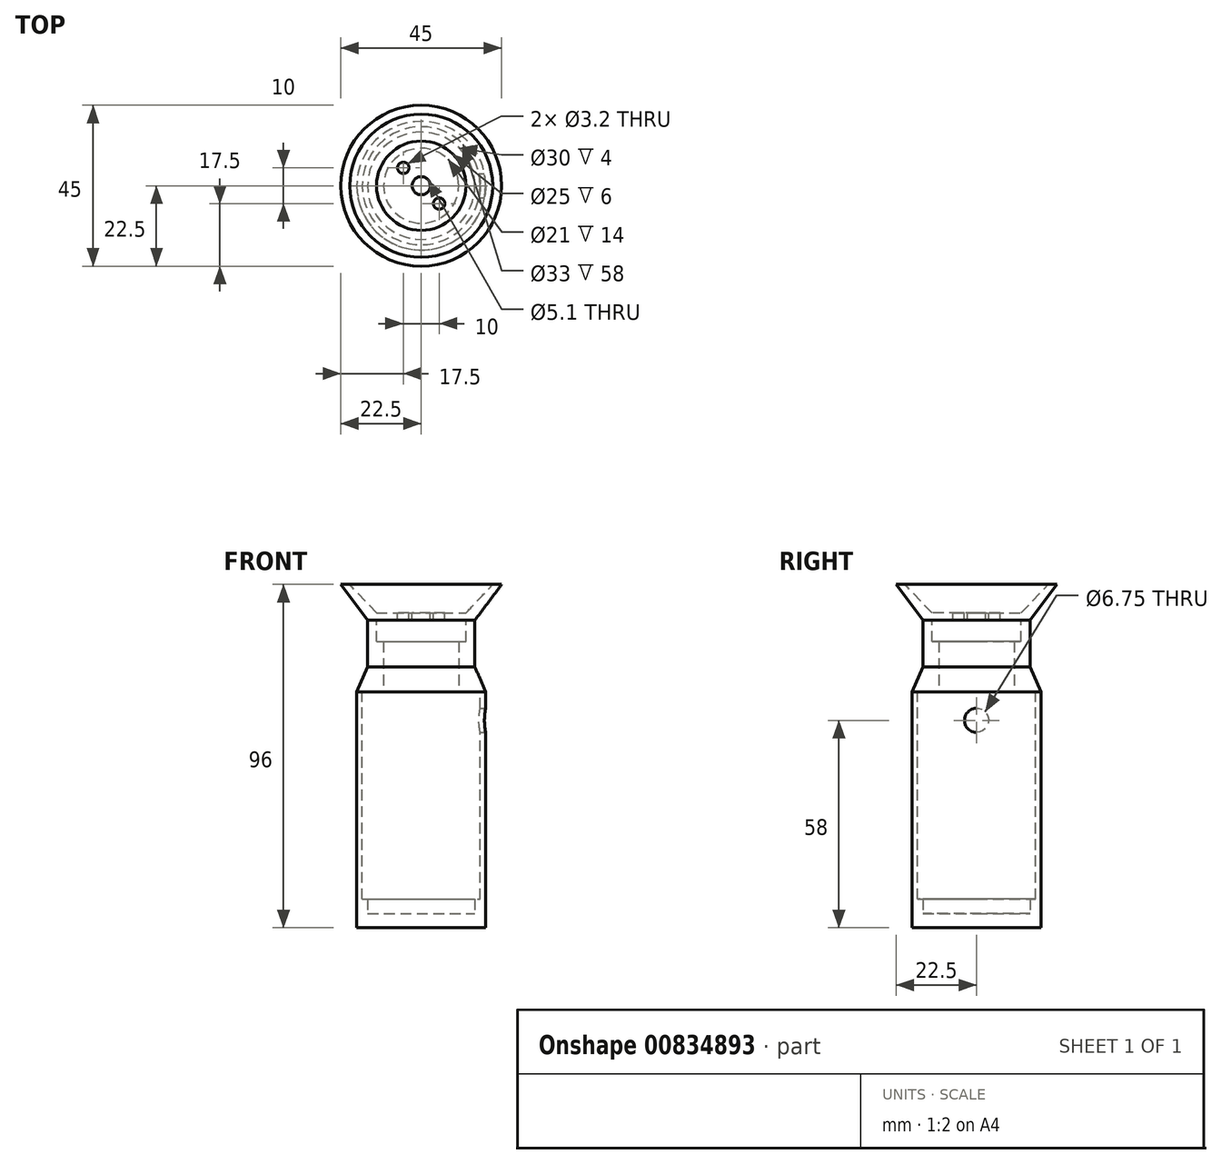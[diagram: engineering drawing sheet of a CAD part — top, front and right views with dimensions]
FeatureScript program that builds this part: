
annotation { "Feature Type Name" : "Feature", "Feature Type Description" : "" }
export const myFeature = defineFeature(function(context is Context, id is Id, definition is map)
    precondition{}
    {
        {
            var Q0;
            Q0=qCreatedBy(makeId("Top.planeOp"),FACE);
            var sketch = newSketch(context, id + "F0", { "sketchPlane" : qUnion([Q0])});
            skCircle(sketch, "E0", {"center": v(0, 0) * mm, "radius": 15 * mm});
            skSolve(sketch);
        }
        {
            var Q0;
            Q0=qCreatedBy(makeId("Top.planeOp"),FACE);
            cPlane(context, id + "F1", {"entities" : qUnion([Q0]), "cplaneType" : CPlaneType.OFFSET, "offset" : 10 * mm, "width" : 150 * mm, "height" : 150 * mm});
        }
        {
            var Q0;
            Q0=qCreatedBy(id+"F1.planeOp",FACE);
            var sketch = newSketch(context, id + "F2", { "sketchPlane" : qUnion([Q0])});
            skCircle(sketch, "E1", {"center": v(0, 0) * mm, "radius": 22.5 * mm});
            skSolve(sketch);
        }
        {
            var Q0;
            Q0=makeQuery(id+"F2.imprint","IMPRINT",FACE,{"disambiguationData":[TD([[makeQuery(id+"F2.imprint","IMPRINT",EDGE,{"derivedFrom":sQuery(id+"F2.wireOp",EDGE,"E1")}),1.0]])]});
            var Q1;
            Q1=makeQuery(id+"F0.imprint","IMPRINT",FACE,{"disambiguationData":[TD([[makeQuery(id+"F0.imprint","IMPRINT",EDGE,{"derivedFrom":sQuery(id+"F0.wireOp",EDGE,"E0")}),1.0]])]});
            loft(context, id + "F3", {"sheetProfilesArray" : [{ "sheetProfileEntities" : qUnion([Q0]) }, { "sheetProfileEntities" : qUnion([Q1]) }]});
        }
        {
            var Q0;
            Q0=makeQuery(id+"F3.opLoft","CAP_FACE",FACE,{"disambiguationData":[OSD([makeQuery(id+"F2.imprint","IMPRINT",FACE,{"disambiguationData":[TD([[makeQuery(id+"F2.imprint","IMPRINT",EDGE,{"derivedFrom":sQuery(id+"F2.wireOp",EDGE,"E1")}),1.0]])]})])],"isStart":true});
            var sketch = newSketch(context, id + "F4", { "sketchPlane" : qUnion([Q0])});
            skCircle(sketch, "E2", {"center": v(0, 0) * mm, "radius": 20 * mm});
            skSolve(sketch);
        }
        {
            var Q0;
            Q0=makeQuery(id+"F3.opLoft","CAP_FACE",FACE,{"disambiguationData":[OSD([makeQuery(id+"F0.imprint","IMPRINT",FACE,{"disambiguationData":[TD([[makeQuery(id+"F0.imprint","IMPRINT",EDGE,{"derivedFrom":sQuery(id+"F0.wireOp",EDGE,"E0")}),1.0]])]})])],"isStart":true});
            cPlane(context, id + "F5", {"entities" : qUnion([Q0]), "cplaneType" : CPlaneType.OFFSET, "offset" : 2 * mm, "oppositeDirection" : true, "width" : 150 * mm, "height" : 150 * mm});
        }
        {
            var Q0;
            Q0=qCreatedBy(id+"F5.planeOp",FACE);
            var sketch = newSketch(context, id + "F6", { "sketchPlane" : qUnion([Q0])});
            skCircle(sketch, "E3", {"center": v(0, 0) * mm, "radius": 12.5 * mm});
            skSolve(sketch);
        }
        {
            var Q1;
            Q1 = qSketchRegion(id + "F6", true);
            var Q2;
            Q2 = qSketchRegion(id + "F4", true);
            loft(context, id + "F7", {"operationType" : NewBodyOperationType.REMOVE, "sheetProfilesArray" : [{ "sheetProfileEntities" : qUnion([Q1]) }, { "sheetProfileEntities" : qUnion([Q2]) }]});
        }
        {
            var Q0;
            Q0=makeQuery(id+"F3.opLoft","CAP_FACE",FACE,{"disambiguationData":[OSD([makeQuery(id+"F0.imprint","IMPRINT",FACE,{"disambiguationData":[TD([[makeQuery(id+"F0.imprint","IMPRINT",EDGE,{"derivedFrom":sQuery(id+"F0.wireOp",EDGE,"E0")}),1.0]])]})])],"isStart":true});
            var sketch = newSketch(context, id + "F8", { "sketchPlane" : qUnion([Q0])});
            skCircle(sketch, "E4", {"center": v(0, 0) * mm, "radius": 12.5 * mm});
            skSolve(sketch);
        }
        {
            var Q0;
            Q0=makeQuery(id+"F8.imprint","IMPRINT",FACE,{"disambiguationData":[TD([[makeQuery(id+"F8.imprint","IMPRINT",EDGE,{"derivedFrom":sQuery(id+"F8.wireOp",EDGE,"E4")}),-1.0]])]});
            extrude(context, id + "F9", {"entities" : qUnion([Q0]), "operationType" : NewBodyOperationType.ADD, "depth" : 13 * mm, "offsetDistance" : 25 * mm});
        }
        {
            var Q0;
            Q0=makeQuery(id+"F9.opExtrude","CAP_FACE",FACE,{"disambiguationData":[OSD([sQuery(id+"F0.wireOp",EDGE,"E0"),sQuery(id+"F8.wireOp",EDGE,"E4")])],"isStart":false});
            var sketch = newSketch(context, id + "F10", { "sketchPlane" : qUnion([Q0])});
            skCircle(sketch, "E5", {"center": v(0, 0) * mm, "radius": 10.5 * mm});
            skSolve(sketch);
        }
        {
            var Q0;
            Q0=makeQuery(id+"F10.imprint","IMPRINT",FACE,{"disambiguationData":[TD([[makeQuery(id+"F10.imprint","IMPRINT",EDGE,{"derivedFrom":sQuery(id+"F10.wireOp",EDGE,"E5")}),-1.0]])]});
            extrude(context, id + "F11", {"entities" : qUnion([Q0]), "oppositeDirection" : true, "depth" : 7 * mm, "offsetDistance" : 25 * mm});
        }
        {
            var Q0;
            Q0=makeQuery(id+"F11.opExtrude","CAP_FACE",FACE,{"disambiguationData":[OSD([sQuery(id+"F8.wireOp",EDGE,"E4"),sQuery(id+"F10.wireOp",EDGE,"E5")])],"isStart":true});
            var sketch = newSketch(context, id + "F12", { "sketchPlane" : qUnion([Q0])});
            skCircle(sketch, "E6", {"center": v(0, 0) * mm, "radius": 15 * mm});
            skCircle(sketch, "E7", {"center": v(0, 0) * mm, "radius": 10.5 * mm});
            skSolve(sketch);
        }
        {
            var Q0;
            Q0=qCreatedBy(makeId("Top.planeOp"),FACE);
            cPlane(context, id + "F13", {"entities" : qUnion([Q0]), "cplaneType" : CPlaneType.OFFSET, "offset" : 20 * mm, "oppositeDirection" : true, "width" : 150 * mm, "height" : 150 * mm});
        }
        {
            var Q0;
            Q0=qCreatedBy(id+"F13.planeOp",FACE);
            var sketch = newSketch(context, id + "F14", { "sketchPlane" : qUnion([Q0])});
            skCircle(sketch, "E8", {"center": v(0, 0) * mm, "radius": 18 * mm});
            skSolve(sketch);
        }
        {
            var Q0;
            Q0=makeQuery(id+"F12.imprint","IMPRINT",FACE,{"disambiguationData":[TD([[makeQuery(id+"F12.imprint","IMPRINT",EDGE,{"derivedFrom":sQuery(id+"F12.wireOp",EDGE,"E6")}),1.0]])]});
            var sketch = newSketch(context, id + "F15", { "sketchPlane" : qUnion([Q0])});
            skCircle(sketch, "E9", {"center": v(0, 0) * mm, "radius": 15 * mm});
            skSolve(sketch);
        }
        {
            var Q1;
            Q1 = qSketchRegion(id + "F14", true);
            var Q2;
            Q2 = qSketchRegion(id + "F15", true);
            loft(context, id + "F16", {"operationType" : NewBodyOperationType.ADD, "sheetProfilesArray" : [{ "sheetProfileEntities" : qUnion([Q1]) }, { "sheetProfileEntities" : qUnion([Q2]) }]});
        }
        {
            var Q0;
            Q0=makeQuery(id+"F16.opLoft","CAP_FACE",FACE,{"disambiguationData":[OSD([makeQuery(id+"F14.imprint","IMPRINT",FACE,{"disambiguationData":[TD([[makeQuery(id+"F14.imprint","IMPRINT",EDGE,{"derivedFrom":sQuery(id+"F14.wireOp",EDGE,"E8")}),1.0]])]})])],"isStart":true});
            var sketch = newSketch(context, id + "F17", { "sketchPlane" : qUnion([Q0])});
            skCircle(sketch, "E10", {"center": v(0, 0) * mm, "radius": 10.5 * mm});
            skSolve(sketch);
        }
        {
            var Q0;
            Q0=makeQuery(id+"F17.imprint","IMPRINT",FACE,{"disambiguationData":[TD([[makeQuery(id+"F17.imprint","IMPRINT",EDGE,{"derivedFrom":sQuery(id+"F17.wireOp",EDGE,"E10")}),1.0]])]});
            var Q1;
            Q1=sQuery(id+"F12.wireOp",EDGE,"E7");
            extrude(context, id + "F18", {"entities" : qUnion([Q0]), "operationType" : NewBodyOperationType.REMOVE, "surfaceOperationType" : NewSurfaceOperationType.ADD, "surfaceEntities" : qUnion([Q1]), "oppositeDirection" : true, "depth" : 10 * mm, "offsetDistance" : 25 * mm});
        }
        {
            var Q0;
            Q0=makeQuery(id+"F16.opLoft","CAP_FACE",FACE,{"disambiguationData":[OSD([makeQuery(id+"F14.imprint","IMPRINT",FACE,{"disambiguationData":[TD([[makeQuery(id+"F14.imprint","IMPRINT",EDGE,{"derivedFrom":sQuery(id+"F14.wireOp",EDGE,"E8")}),1.0]])]})])],"isStart":true});
            var sketch = newSketch(context, id + "F19", { "sketchPlane" : qUnion([Q0])});
            skCircle(sketch, "E11", {"center": v(0, 0) * mm, "radius": 16.5 * mm});
            skSolve(sketch);
        }
        {
            var Q0;
            Q0=makeQuery(id+"F19.imprint","IMPRINT",FACE,{"disambiguationData":[TD([[makeQuery(id+"F19.imprint","IMPRINT",EDGE,{"derivedFrom":sQuery(id+"F19.wireOp",EDGE,"E11")}),-1.0]])]});
            extrude(context, id + "F20", {"entities" : qUnion([Q0]), "operationType" : NewBodyOperationType.ADD, "depth" : 62 * mm, "offsetDistance" : 25 * mm});
        }
        {
            var Q0;
            Q0=makeQuery(id+"F20.opExtrude","CAP_FACE",FACE,{"disambiguationData":[OSD([sQuery(id+"F14.wireOp",EDGE,"E8"),sQuery(id+"F19.wireOp",EDGE,"E11")])],"isStart":false});
            var sketch = newSketch(context, id + "F21", { "sketchPlane" : qUnion([Q0])});
            skCircle(sketch, "E12", {"center": v(0, 0) * mm, "radius": 15 * mm});
            skSolve(sketch);
        }
        {
            var Q0;
            Q0=makeQuery(id+"F21.imprint","IMPRINT",FACE,{"disambiguationData":[TD([[makeQuery(id+"F21.imprint","IMPRINT",EDGE,{"derivedFrom":sQuery(id+"F21.wireOp",EDGE,"E12")}),-1.0]])]});
            extrude(context, id + "F22", {"entities" : qUnion([Q0]), "oppositeDirection" : true, "depth" : 4 * mm, "offsetDistance" : 25 * mm});
        }
        {
            var Q0;
            Q0=makeQuery(id+"F22.opExtrude","CAP_FACE",FACE,{"disambiguationData":[OSD([sQuery(id+"F19.wireOp",EDGE,"E11"),sQuery(id+"F21.wireOp",EDGE,"E12")])],"isStart":true});
            extrude(context, id + "F23", {"entities" : qUnion([Q0]), "operationType" : NewBodyOperationType.ADD, "depth" : 4 * mm, "offsetDistance" : 25 * mm});
        }
        {
            var Q0;
            Q0=makeQuery(id+"F23.opExtrude","CAP_FACE",FACE,{"disambiguationData":[OSD([sQuery(id+"F19.wireOp",EDGE,"E11"),sQuery(id+"F21.wireOp",EDGE,"E12")])],"isStart":false});
            var sketch = newSketch(context, id + "F24", { "sketchPlane" : qUnion([Q0])});
            skCircle(sketch, "E13", {"center": v(0, 0) * mm, "radius": 18 * mm});
            skSolve(sketch);
        }
        {
            var Q0;
            Q0=makeQuery(id+"F24.imprint","IMPRINT",FACE,{"disambiguationData":[TD([[makeQuery(id+"F24.imprint","IMPRINT",EDGE,{"derivedFrom":sQuery(id+"F24.wireOp",EDGE,"E13")}),1.0]])]});
            var Q1;
            Q1=makeQuery(id+"F24.imprint","IMPRINT",FACE,{"disambiguationData":[TD([[makeQuery(id+"F24.imprint","IMPRINT",EDGE,{"derivedFrom":makeQuery(id+"F23.opExtrude","CAP_EDGE",EDGE,{"disambiguationData":[OSD([sQuery(id+"F21.wireOp",EDGE,"E12")])],"isStart":false})}),1.0]])]});
            var Q2;
            Q2=sQuery(id+"F24.wireOp",EDGE,"E13");
            extrude(context, id + "F25", {"entities" : qUnion([Q0, Q1]), "operationType" : NewBodyOperationType.ADD, "surfaceOperationType" : NewSurfaceOperationType.ADD, "surfaceEntities" : qUnion([Q2]), "oppositeDirection" : true, "depth" : 4 * mm, "offsetDistance" : 25 * mm});
        }
        {
            var Q0;
            Q0=makeQuery(id+"F7.boolean.opBoolean","COPY",FACE,{"derivedFrom":makeQuery(id+"F7.opLoft","CAP_FACE",FACE,{"disambiguationData":[OSD([makeQuery(id+"F6.imprint","IMPRINT",FACE,{"disambiguationData":[TD([[makeQuery(id+"F6.imprint","IMPRINT",EDGE,{"derivedFrom":sQuery(id+"F6.wireOp",EDGE,"E3")}),1.0]])]})])],"isStart":true})});
            var sketch = newSketch(context, id + "F26", { "sketchPlane" : qUnion([Q0])});
            skCircle(sketch, "E14", {"center": v(0, 0) * mm, "radius": 2.55 * mm});
            skCircle(sketch, "E15", {"center": v(-5, 5) * mm, "radius": 1.6 * mm});
            skCircle(sketch, "E16", {"center": v(5, -5) * mm, "radius": 1.6 * mm});
            skSolve(sketch);
        }
        {
            var Q0;
            Q0 = qSketchRegion(id + "F26", true);
            extrude(context, id + "F27", {"entities" : qUnion([Q0]), "operationType" : NewBodyOperationType.REMOVE, "oppositeDirection" : true, "depth" : 3 * mm, "offsetDistance" : 25 * mm});
        }
        {
            var Q0;
            Q0=qCreatedBy(makeId("Right.planeOp"),FACE);
            cPlane(context, id + "F28", {"entities" : qUnion([Q0]), "cplaneType" : CPlaneType.OFFSET, "offset" : 18 * mm, "width" : 150 * mm, "height" : 150 * mm});
        }
        {
            var Q0;
            Q0=qCreatedBy(id+"F28.planeOp",FACE);
            var sketch = newSketch(context, id + "F29", { "sketchPlane" : qUnion([Q0])});
            skCircle(sketch, "E17", {"center": v(0, -28) * mm, "radius": 3.37 * mm});
            skSolve(sketch);
        }
        {
            var Q0;
            Q0 = qSketchRegion(id + "F29", true);
            extrude(context, id + "F30", {"entities" : qUnion([Q0]), "operationType" : NewBodyOperationType.REMOVE, "oppositeDirection" : true, "depth" : 4 * mm, "offsetDistance" : 25 * mm});
        }
    });
